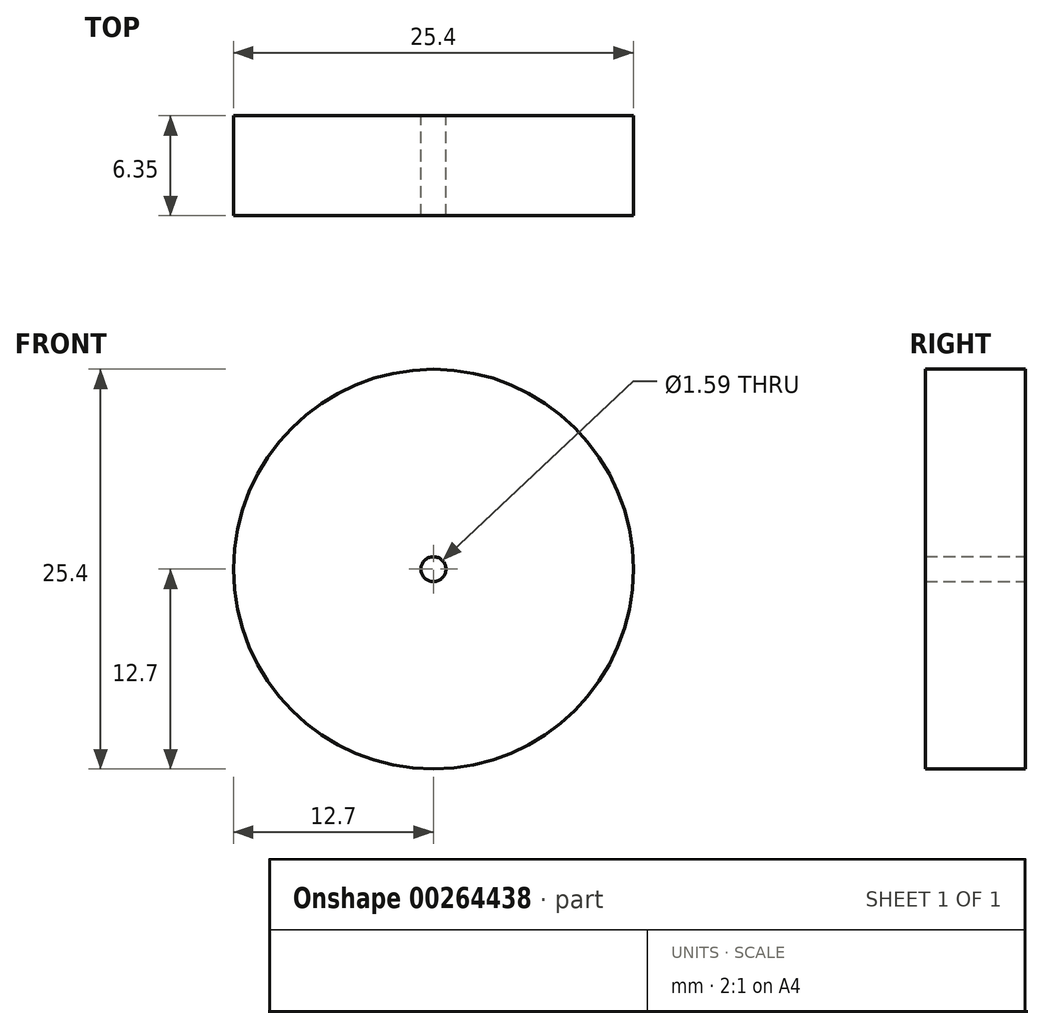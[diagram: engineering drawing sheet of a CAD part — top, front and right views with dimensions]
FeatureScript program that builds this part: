
annotation { "Feature Type Name" : "Feature", "Feature Type Description" : "" }
export const myFeature = defineFeature(function(context is Context, id is Id, definition is map)
    precondition{}
    {
        {
            var Q0;
            Q0=qCreatedBy(makeId("Front.planeOp"),FACE);
            var sketch = newSketch(context, id + "F0", { "sketchPlane" : qUnion([Q0])});
            skCircle(sketch, "E0", {"center": v(0, 0) * mm, "radius": 12.7 * mm});
            skCircle(sketch, "E1", {"center": v(0, 0) * mm, "radius": 0.8 * mm});
            skSolve(sketch);
        }
        {
            var Q0;
            Q0=qSketchRegion(id+"F0",true);
            extrude(context, id + "F1", {"entities" : qUnion([Q0]), "depth" : 6.35 * mm});
        }
    });
